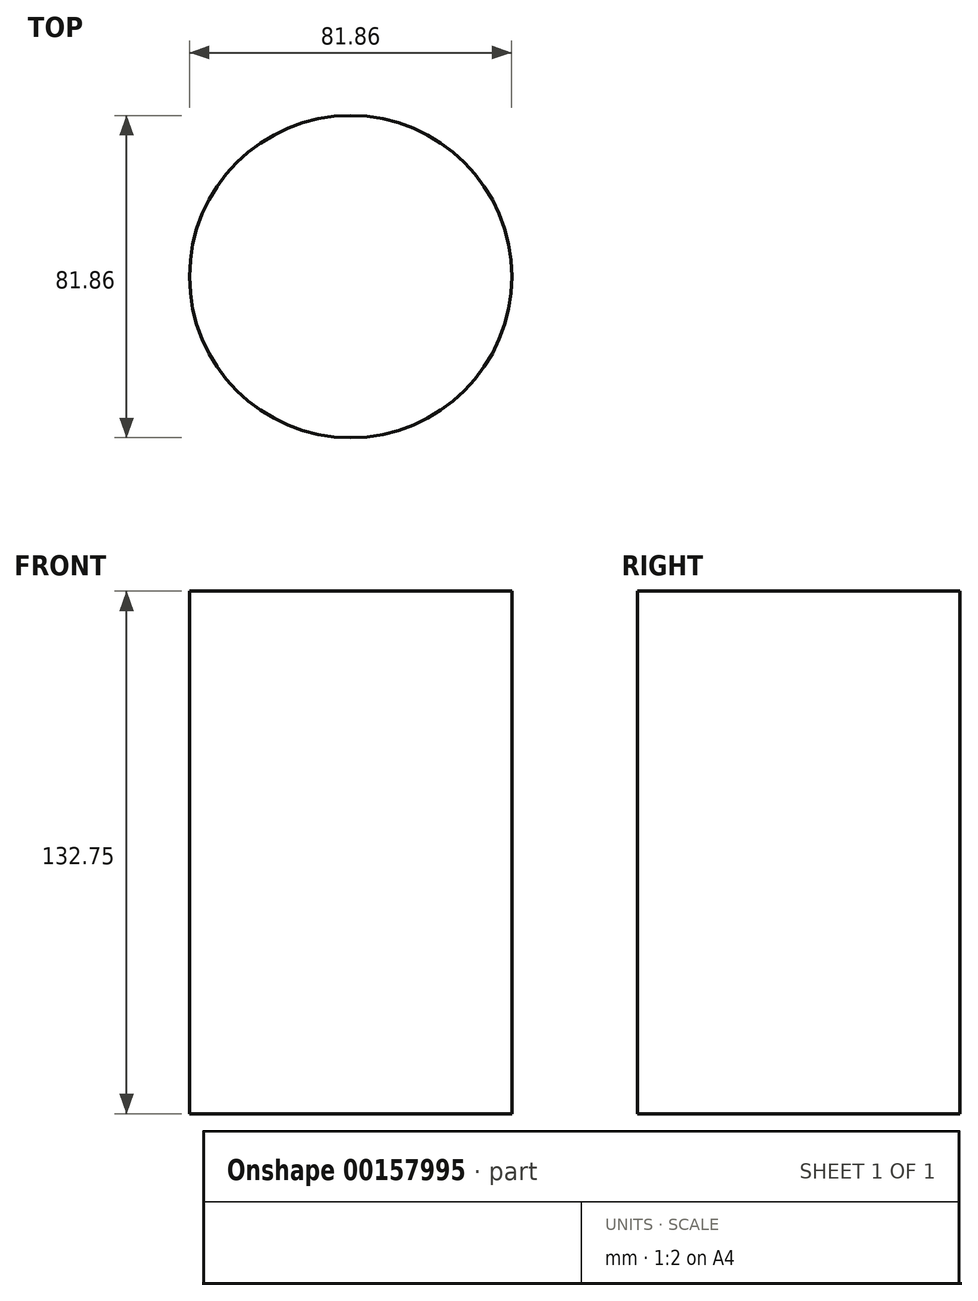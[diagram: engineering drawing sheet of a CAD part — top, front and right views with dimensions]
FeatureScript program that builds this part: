
annotation { "Feature Type Name" : "Feature", "Feature Type Description" : "" }
export const myFeature = defineFeature(function(context is Context, id is Id, definition is map)
    precondition{}
    {
        {
            var Q0;
            Q0=qCreatedBy(makeId("Top.planeOp"),FACE);
            var sketch = newSketch(context, id + "F0", { "sketchPlane" : qUnion([Q0])});
            skCircle(sketch, "E0", {"center": v(0, 0) * mm, "radius": 40.93 * mm});
            skCircle(sketch, "E1", {"center": v(0, 0) * mm, "radius": 5.78 * mm});
            skCircle(sketch, "E2", {"center": v(0, 0) * mm, "radius": 33.49 * mm});
            skCircle(sketch, "E3", {"center": v(0, 0) * mm, "radius": 22.2 * mm});
            skSolve(sketch);
        }
        {
            var Q0;
            Q0=makeQuery(id+"F0.imprint","IMPRINT",FACE,{"disambiguationData":[TD([[makeQuery(id+"F0.imprint","IMPRINT",EDGE,{"derivedFrom":sQuery(id+"F0.wireOp",EDGE,"E0")}),1.0]])]});
            var Q1;
            Q1=makeQuery(id+"F0.imprint","IMPRINT",FACE,{"disambiguationData":[TD([[makeQuery(id+"F0.imprint","IMPRINT",EDGE,{"derivedFrom":sQuery(id+"F0.wireOp",EDGE,"E2")}),1.0]])]});
            var Q2;
            Q2=makeQuery(id+"F0.imprint","IMPRINT",FACE,{"disambiguationData":[TD([[makeQuery(id+"F0.imprint","IMPRINT",EDGE,{"derivedFrom":sQuery(id+"F0.wireOp",EDGE,"E1")}),-1.0]])]});
            var Q3;
            Q3=makeQuery(id+"F0.imprint","IMPRINT",FACE,{"disambiguationData":[TD([[makeQuery(id+"F0.imprint","IMPRINT",EDGE,{"derivedFrom":sQuery(id+"F0.wireOp",EDGE,"E1")}),1.0]])]});
            extrude(context, id + "F1", {"entities" : qUnion([Q0, Q1, Q2, Q3]), "depth" : 132.75 * mm});
        }
        {
            var Q0;
            Q0=makeQuery(id+"F0.imprint","IMPRINT",FACE,{"disambiguationData":[TD([[makeQuery(id+"F0.imprint","IMPRINT",EDGE,{"derivedFrom":sQuery(id+"F0.wireOp",EDGE,"E1")}),1.0]])]});
            extrude(context, id + "F2", {"entities" : qUnion([Q0]), "operationType" : NewBodyOperationType.ADD, "depth" : 25 * mm});
        }
    });
